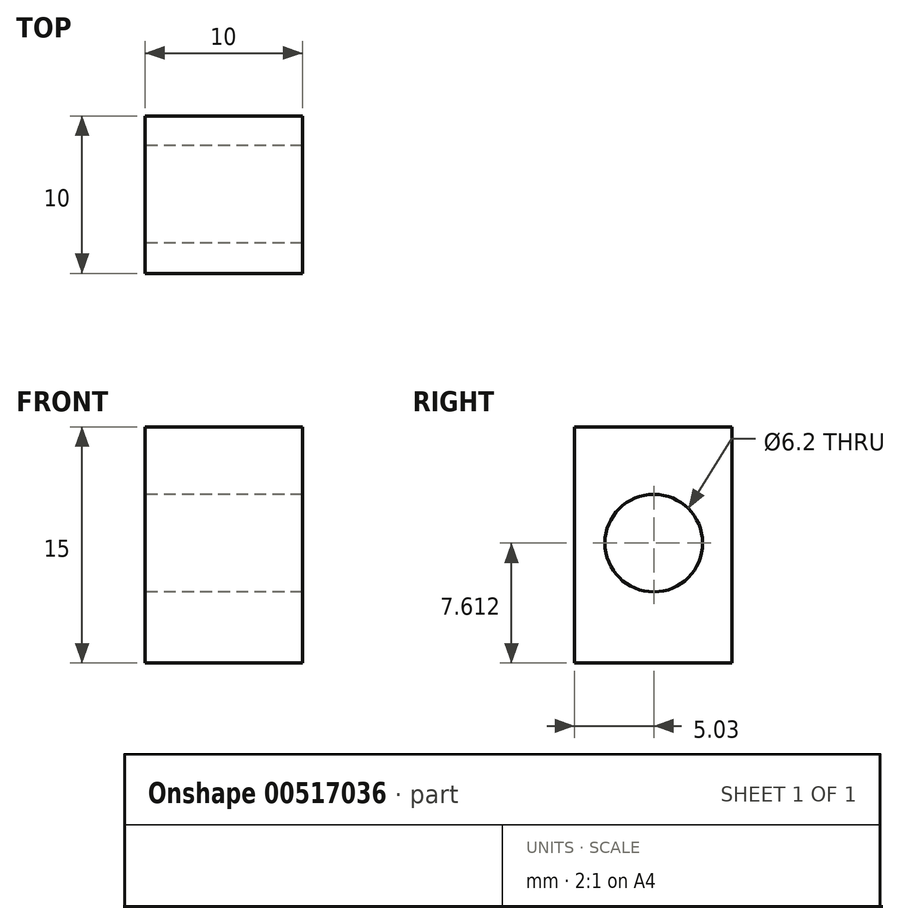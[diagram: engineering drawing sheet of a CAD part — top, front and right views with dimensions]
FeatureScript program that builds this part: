
annotation { "Feature Type Name" : "Feature", "Feature Type Description" : "" }
export const myFeature = defineFeature(function(context is Context, id is Id, definition is map)
    precondition{}
    {
        {
            var Q0;
            Q0=qCreatedBy(makeId("Front.planeOp"),FACE);
            var sketch = newSketch(context, id + "F0", { "sketchPlane" : qUnion([Q0])});
            skLineSegment(sketch, "E0.bottom", {"start": v(0, 0) * mm, "end": v(10, 0) * mm});
            skLineSegment(sketch, "E0.top", {"start": v(0, 15) * mm, "end": v(10, 15) * mm});
            skLineSegment(sketch, "E0.left", {"start": v(0, 0) * mm, "end": v(0, 15) * mm});
            skLineSegment(sketch, "E0.right", {"start": v(10, 0) * mm, "end": v(10, 15) * mm});
            skSolve(sketch);
        }
        {
            var Q0;
            Q0 = qSketchRegion(id + "F0", true);
            extrude(context, id + "F1", {"entities" : qUnion([Q0]), "depth" : 10 * mm, "offsetDistance" : 25 * mm});
        }
        {
            var Q0;
            Q0=makeQuery(id+"F1.opExtrude","SWEPT_FACE",FACE,{"disambiguationData":[OSD([sQuery(id+"F0.wireOp",EDGE,"E0.left")])]});
            var sketch = newSketch(context, id + "F2", { "sketchPlane" : qUnion([Q0])});
            skCircle(sketch, "E1", {"center": v(4.97, 7.61) * mm, "radius": 3.1 * mm});
            skSolve(sketch);
        }
        {
            var Q0;
            Q0=sQuery(id+"F2.wireOp",VERTEX,"E1.center");
            var Q1;
            Q1=makeQuery(id+"F1.opExtrude","SWEPT_BODY",BODY,{"disambiguationData":[OSD([sQuery(id+"F0.wireOp",EDGE,"E0.bottom"),sQuery(id+"F0.wireOp",EDGE,"E0.top"),sQuery(id+"F0.wireOp",EDGE,"E0.left"),sQuery(id+"F0.wireOp",EDGE,"E0.right")])]});
            hole(context, id + "F3", {"style" : HoleStyle.SIMPLE, "endStyle" : HoleEndStyle.THROUGH, "holeDiameter" : 6.2 * mm, "isTappedThrough" : true, "tappedDepth" : 12 * mm, "tapClearance" : 3, "locations" : qUnion([Q0]), "scope" : qUnion([Q1])});
        }
    });
